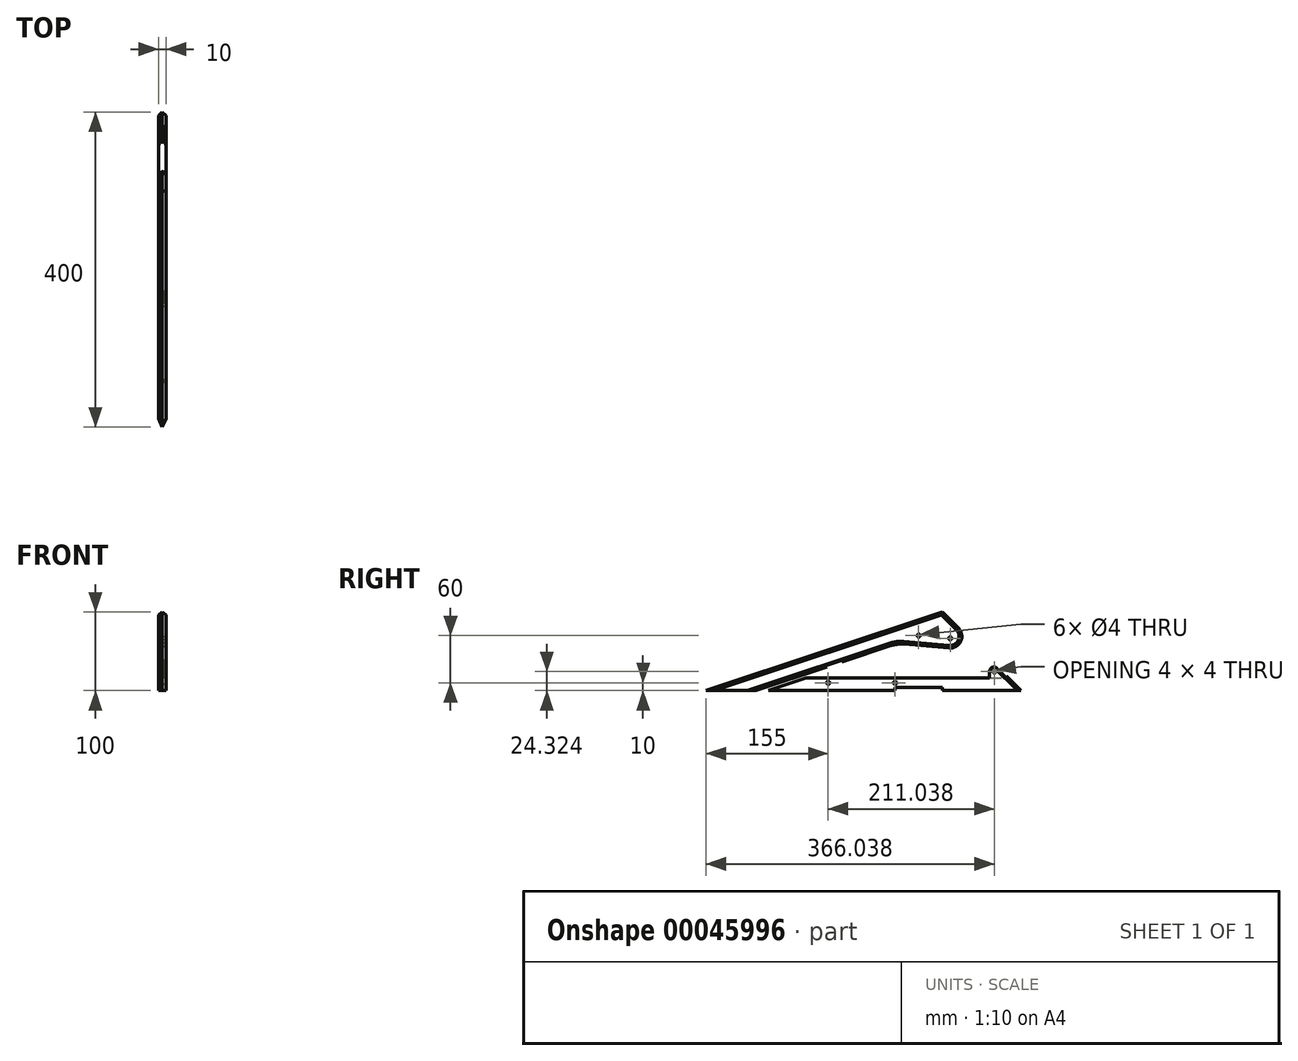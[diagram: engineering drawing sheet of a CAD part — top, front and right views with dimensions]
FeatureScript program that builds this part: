
annotation { "Feature Type Name" : "Feature", "Feature Type Description" : "" }
export const myFeature = defineFeature(function(context is Context, id is Id, definition is map)
    precondition{}
    {
        {
            var Q0;
            Q0=qCreatedBy(makeId("Right.planeOp"),FACE);
            var sketch = newSketch(context, id + "F0", { "sketchPlane" : qUnion([Q0])});
            skLineSegment(sketch, "E0", {"start": v(100, 100) * mm, "end": v(-200, 0) * mm});
            skLineSegment(sketch, "E1", {"start": v(-120.94, 0) * mm, "end": v(-72.94, 16) * mm});
            skLineSegment(sketch, "E2", {"start": v(-136.75, 0) * mm, "end": v(-200, 0) * mm});
            skLineSegment(sketch, "E3", {"start": v(40, 0) * mm, "end": v(40, 48.47) * mm, "construction": true});
            skLineSegment(sketch, "E4", {"start": v(-144.52, 10) * mm, "end": v(224.52, 10) * mm, "construction": true});
            skPoint(sketch, "E5", {"position": v(40, 10) * mm});
            skLineSegment(sketch, "E6", {"start": v(70, 119.46) * mm, "end": v(70, 39.46) * mm, "construction": true});
            skPoint(sketch, "E7", {"position": v(70, 79.46) * mm});
            skLineSegment(sketch, "E8", {"start": v(-168.38, 0) * mm, "end": v(107.9, 92.1) * mm, "construction": true});
            skLineSegment(sketch, "E9", {"start": v(-45, 56.15) * mm, "end": v(-45, -36.15) * mm, "construction": true});
            skPoint(sketch, "E10", {"position": v(-45, 10) * mm});
            skCircle(sketch, "E11", {"center": v(-45, 10) * mm, "radius": 2 * mm});
            skLineSegment(sketch, "E12", {"start": v(-45.95, 60.64) * mm, "end": v(-34.05, 24.95) * mm, "construction": true});
            skPoint(sketch, "E13", {"position": v(-40, 42.8) * mm});
            skLineSegment(sketch, "E14", {"start": v(200, 0) * mm, "end": v(170, 30) * mm});
            skLineSegment(sketch, "E15", {"start": v(-229.72, 0) * mm, "end": v(246.05, 0) * mm, "construction": true});
            skLineSegment(sketch, "E16", {"start": v(51.02, 59.11) * mm, "end": v(108.45, 54.09) * mm});
            skPoint(sketch, "E17.visualSharp", {"position": v(42.75, 59.84) * mm});
            skArc(sketch, "E17.filletArc", {"start": v(51.02, 59.11) * mm, "mid": v(42.85, 59) * mm, "end": v(34.88, 57.21) * mm});
            skPoint(sketch, "E18", {"position": v(70, 70) * mm});
            skLineSegment(sketch, "E19", {"start": v(14.84, 70) * mm, "end": v(125.16, 70) * mm, "construction": true});
            skCircle(sketch, "E20", {"center": v(70, 70) * mm, "radius": 2 * mm});
            skLineSegment(sketch, "E21", {"start": v(-120.94, 0) * mm, "end": v(40, 0) * mm});
            skLineSegment(sketch, "E22", {"start": v(40, 0) * mm, "end": v(40, 4) * mm});
            skLineSegment(sketch, "E23", {"start": v(40, 4) * mm, "end": v(100, 4) * mm});
            skLineSegment(sketch, "E24", {"start": v(100, 4) * mm, "end": v(100, 0) * mm});
            skLineSegment(sketch, "E25", {"start": v(100, 0) * mm, "end": v(200, 0) * mm});
            skLineSegment(sketch, "E26", {"start": v(-72.94, 16) * mm, "end": v(160.04, 16) * mm});
            skLineSegment(sketch, "E27", {"start": v(100, 100) * mm, "end": v(200, 0) * mm, "construction": true});
            skLineSegment(sketch, "E28", {"start": v(120.36, 79.64) * mm, "end": v(100, 100) * mm});
            skLineSegment(sketch, "E29", {"start": v(170, 30) * mm, "end": v(166.56, 30.3) * mm});
            skLineSegment(sketch, "E30", {"start": v(160.04, 24.32) * mm, "end": v(160.04, 16) * mm});
            skPoint(sketch, "E31.visualSharp", {"position": v(160.04, 30.87) * mm});
            skArc(sketch, "E31.filletArc", {"start": v(166.56, 30.3) * mm, "mid": v(161.98, 28.75) * mm, "end": v(160.04, 24.32) * mm});
            skCircle(sketch, "E32", {"center": v(166.04, 24.32) * mm, "radius": 2 * mm});
            skLineSegment(sketch, "E33", {"start": v(-136.75, 0) * mm, "end": v(-46.32, 30.14) * mm});
            skLineSegment(sketch, "E34", {"start": v(-46.32, 30.14) * mm, "end": v(-46.96, 32.04) * mm});
            skLineSegment(sketch, "E35", {"start": v(-46.96, 32.04) * mm, "end": v(-27.98, 38.37) * mm});
            skLineSegment(sketch, "E36", {"start": v(-27.98, 38.37) * mm, "end": v(-27.35, 36.47) * mm});
            skLineSegment(sketch, "E37", {"start": v(-27.35, 36.47) * mm, "end": v(34.88, 57.21) * mm});
            skPoint(sketch, "E38", {"position": v(-37.47, 35.2) * mm});
            skLineSegment(sketch, "E39", {"start": v(14.88, 74.82) * mm, "end": v(129.4, 64.8) * mm, "construction": true});
            skCircle(sketch, "E40", {"center": v(110, 66.5) * mm, "radius": 2 * mm});
            skPoint(sketch, "E41.visualSharp", {"position": v(149.5, 50.5) * mm});
            skArc(sketch, "E41.filletArc", {"start": v(108.45, 54.09) * mm, "mid": v(123.35, 62.7) * mm, "end": v(120.36, 79.64) * mm});
            skCircle(sketch, "E42", {"center": v(40, 10) * mm, "radius": 2 * mm});
            skSolve(sketch);
        }
        {
            var Q0;
            Q0=makeQuery(id+"F0.imprint","IMPRINT",FACE,{"disambiguationData":[TD([[makeQuery(id+"F0.imprint","IMPRINT",EDGE,{"derivedFrom":sQuery(id+"F0.wireOp",EDGE,"E0")}),1.0]])]});
            extrude(context, id + "F1", {"entities" : qUnion([Q0]), "depth" : 10 * mm});
        }
        {
            var Q0;
            Q0=makeQuery(id+"F0.imprint","IMPRINT",FACE,{"disambiguationData":[TD([[makeQuery(id+"F0.imprint","IMPRINT",EDGE,{"derivedFrom":sQuery(id+"F0.wireOp",EDGE,"E1")}),-1.0]])]});
            extrude(context, id + "F2", {"entities" : qUnion([Q0]), "depth" : 10 * mm});
        }
        {
            var Q0;
            Q0=makeQuery(id+"F1.opExtrude","CAP_EDGE",EDGE,{"disambiguationData":[OSD([sQuery(id+"F0.wireOp",EDGE,"E0")])],"isStart":false});
            chamfer(context, id + "F3", {"entities" : qUnion([Q0]), "chamferType" : ChamferType.OFFSET_ANGLE, "width" : 5 * mm, "oppositeDirection" : true, "angle" : 33.7 * degree, "tangentPropagation" : true});
        }
        {
            var Q0;
            Q0=makeQuery(id+"F1.opExtrude","CAP_EDGE",EDGE,{"disambiguationData":[OSD([sQuery(id+"F0.wireOp",EDGE,"E0")])],"isStart":true});
            chamfer(context, id + "F4", {"entities" : qUnion([Q0]), "chamferType" : ChamferType.OFFSET_ANGLE, "width" : 5 * mm, "oppositeDirection" : false, "angle" : 33.7 * degree, "tangentPropagation" : true});
        }
        {
            var Q0;
            Q0=makeQuery(id+"F1.opExtrude","CAP_EDGE",EDGE,{"disambiguationData":[OSD([sQuery(id+"F0.wireOp",EDGE,"E28")])],"isStart":true});
            var Q1;
            Q1=makeQuery(id+"F1.opExtrude","CAP_EDGE",EDGE,{"disambiguationData":[OSD([sQuery(id+"F0.wireOp",EDGE,"E28")])],"isStart":false});
            chamfer(context, id + "F5", {"entities" : qUnion([Q0, Q1]), "chamferType" : ChamferType.OFFSET_ANGLE, "width" : 5 * mm, "oppositeDirection" : false, "angle" : 33.7 * degree, "tangentPropagation" : true});
        }
        {
            var Q0;
            Q0=makeQuery(id+"F2.opExtrude","CAP_EDGE",EDGE,{"disambiguationData":[OSD([sQuery(id+"F0.wireOp",EDGE,"E14")])],"isStart":true});
            var Q1;
            Q1=makeQuery(id+"F2.opExtrude","CAP_EDGE",EDGE,{"disambiguationData":[OSD([sQuery(id+"F0.wireOp",EDGE,"E14")])],"isStart":false});
            chamfer(context, id + "F6", {"entities" : qUnion([Q0, Q1]), "chamferType" : ChamferType.OFFSET_ANGLE, "width" : 5 * mm, "oppositeDirection" : false, "angle" : 33.7 * degree, "tangentPropagation" : true});
        }
        {
            var Q0;
            Q0=makeQuery(id+"F2.opExtrude","SWEPT_FACE",FACE,{"disambiguationData":[OSD([sQuery(id+"F0.wireOp",EDGE,"E26")])]});
            var sketch = newSketch(context, id + "F7", { "sketchPlane" : qUnion([Q0])});
            skLineSegment(sketch, "E43.rect.bottom", {"start": v(7.5, 151.56) * mm, "end": v(2.5, 151.56) * mm});
            skLineSegment(sketch, "E43.rect.top", {"start": v(7.5, 181.56) * mm, "end": v(2.5, 181.56) * mm});
            skLineSegment(sketch, "E43.rect.left", {"start": v(7.5, 151.56) * mm, "end": v(7.5, 181.56) * mm});
            skLineSegment(sketch, "E43.rect.right", {"start": v(2.5, 151.56) * mm, "end": v(2.5, 181.56) * mm});
            skPoint(sketch, "E43.rect.middle", {"position": v(5, 166.56) * mm});
            skSolve(sketch);
        }
        {
            var Q0;
            Q0 = qSketchRegion(id + "F7", true);
            extrude(context, id + "F8", {"entities" : qUnion([Q0]), "operationType" : NewBodyOperationType.REMOVE, "depth" : 25 * mm});
        }
    });
